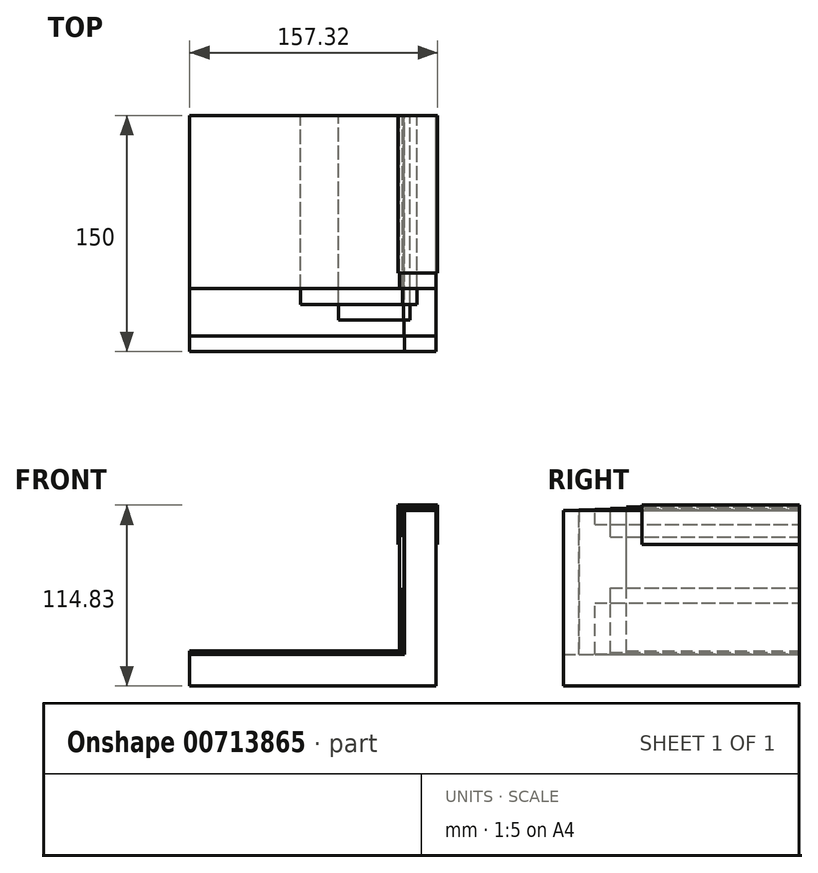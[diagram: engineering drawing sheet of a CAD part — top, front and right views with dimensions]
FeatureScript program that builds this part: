
annotation { "Feature Type Name" : "Feature", "Feature Type Description" : "" }
export const myFeature = defineFeature(function(context is Context, id is Id, definition is map)
    precondition{}
    {
        {
            var Q0;
            Q0=qCreatedBy(makeId("Front.planeOp"),FACE);
            var sketch = newSketch(context, id + "F0", { "sketchPlane" : qUnion([Q0])});
            skLineSegment(sketch, "E0", {"start": v(-78.43, -35.74) * mm, "end": v(-78.43, -55.74) * mm});
            skLineSegment(sketch, "E1", {"start": v(-78.43, -55.74) * mm, "end": v(77.9, -55.74) * mm});
            skLineSegment(sketch, "E2", {"start": v(77.9, -55.74) * mm, "end": v(77.9, 55.9) * mm});
            skLineSegment(sketch, "E3", {"start": v(77.9, 55.9) * mm, "end": v(57.9, 55.9) * mm});
            skLineSegment(sketch, "E4", {"start": v(57.9, 55.9) * mm, "end": v(57.9, -35.74) * mm});
            skLineSegment(sketch, "E5", {"start": v(57.9, -35.74) * mm, "end": v(-78.43, -35.74) * mm});
            skLineSegment(sketch, "E6", {"start": v(-78.43, -35.74) * mm, "end": v(-78.43, -35.54) * mm});
            skLineSegment(sketch, "E7", {"start": v(-78.43, -35.54) * mm, "end": v(57.7, -35.54) * mm});
            skLineSegment(sketch, "E8", {"start": v(57.7, -35.54) * mm, "end": v(57.7, 56.1) * mm});
            skLineSegment(sketch, "E9", {"start": v(57.7, 56.1) * mm, "end": v(77.9, 56.1) * mm});
            skLineSegment(sketch, "E10", {"start": v(77.9, 56.1) * mm, "end": v(77.9, 55.9) * mm});
            skLineSegment(sketch, "E11", {"start": v(16.06, -35.54) * mm, "end": v(16.06, -35.24) * mm});
            skLineSegment(sketch, "E12", {"start": v(16.06, -35.24) * mm, "end": v(57.4, -35.24) * mm});
            skLineSegment(sketch, "E13", {"start": v(57.4, -35.24) * mm, "end": v(57.4, -3.1) * mm});
            skLineSegment(sketch, "E14", {"start": v(57.4, -3.1) * mm, "end": v(57.7, -3.1) * mm});
            skLineSegment(sketch, "E15", {"start": v(-8.23, -35.54) * mm, "end": v(-8.23, -34.54) * mm});
            skLineSegment(sketch, "E16", {"start": v(-8.23, -34.54) * mm, "end": v(56.7, -34.54) * mm});
            skLineSegment(sketch, "E17", {"start": v(56.7, -34.54) * mm, "end": v(56.7, 6.5) * mm});
            skLineSegment(sketch, "E18", {"start": v(56.7, 6.5) * mm, "end": v(57.7, 6.5) * mm});
            skLineSegment(sketch, "E19", {"start": v(57.7, 46.7) * mm, "end": v(57.4, 46.7) * mm});
            skLineSegment(sketch, "E20", {"start": v(57.4, 46.7) * mm, "end": v(57.4, 56.4) * mm});
            skLineSegment(sketch, "E21", {"start": v(57.4, 56.4) * mm, "end": v(61.57, 56.4) * mm});
            skLineSegment(sketch, "E22", {"start": v(61.57, 56.4) * mm, "end": v(61.57, 56.1) * mm});
            skLineSegment(sketch, "E23", {"start": v(57.7, 38.95) * mm, "end": v(56.7, 38.95) * mm});
            skLineSegment(sketch, "E24", {"start": v(56.7, 38.95) * mm, "end": v(56.7, 57.1) * mm});
            skLineSegment(sketch, "E25", {"start": v(56.7, 57.1) * mm, "end": v(65.85, 57.1) * mm});
            skLineSegment(sketch, "E26", {"start": v(65.85, 57.1) * mm, "end": v(65.85, 56.1) * mm});
            skLineSegment(sketch, "E27", {"start": v(-78.43, -35.54) * mm, "end": v(-78.43, -33.54) * mm});
            skLineSegment(sketch, "E28", {"start": v(-78.43, -33.54) * mm, "end": v(54.7, -33.54) * mm});
            skLineSegment(sketch, "E29", {"start": v(54.7, -33.54) * mm, "end": v(54.7, 58.1) * mm});
            skLineSegment(sketch, "E30", {"start": v(54.7, 58.1) * mm, "end": v(77.9, 58.1) * mm});
            skLineSegment(sketch, "E31", {"start": v(77.9, 58.1) * mm, "end": v(77.9, 56.1) * mm});
            skLineSegment(sketch, "E32", {"start": v(54.7, 34.1) * mm, "end": v(53.7, 34.1) * mm});
            skLineSegment(sketch, "E33", {"start": v(53.7, 34.1) * mm, "end": v(53.7, 59.1) * mm});
            skLineSegment(sketch, "E34", {"start": v(53.7, 59.1) * mm, "end": v(78.9, 59.1) * mm});
            skLineSegment(sketch, "E35", {"start": v(78.9, 59.1) * mm, "end": v(78.9, 34.1) * mm});
            skLineSegment(sketch, "E36", {"start": v(78.9, 34.1) * mm, "end": v(77.9, 34.1) * mm});
            skSolve(sketch);
        }
        {
            var Q0;
            Q0=makeQuery(id+"F0.imprint","IMPRINT",FACE,{"disambiguationData":[TD([[makeQuery(id+"F0.imprint","IMPRINT",EDGE,{"derivedFrom":sQuery(id+"F0.wireOp",EDGE,"E0")}),1.0]])]});
            extrude(context, id + "F1", {"entities" : qUnion([Q0]), "depth" : 150 * mm});
        }
        {
            var Q0;
            Q0=makeQuery(id+"F0.imprint","IMPRINT",FACE,{"disambiguationData":[TD([[makeQuery(id+"F0.imprint","IMPRINT",EDGE,{"derivedFrom":sQuery(id+"F0.wireOp",EDGE,"E3")}),-1.0]])]});
            extrude(context, id + "F2", {"entities" : qUnion([Q0]), "depth" : 140 * mm});
        }
        {
            var Q0;
            {var subQ3=sQuery(id+"F0.wireOp",EDGE,"E11");Q0=makeQuery(id+"F0.imprint","IMPRINT",FACE,{"disambiguationData":[TD([[makeQuery(id+"F0.imprint","IMPRINT",EDGE,{"derivedFrom":subQ3}),-1.0]])]});}
            extrude(context, id + "F3", {"entities" : qUnion([Q0]), "depth" : 130 * mm});
        }
        {
            var Q0;
            {var subQ0=sQuery(id+"F0.wireOp",EDGE,"E19");Q0=makeQuery(id+"F0.imprint","IMPRINT",FACE,{"disambiguationData":[TD([[makeQuery(id+"F0.imprint","IMPRINT",EDGE,{"derivedFrom":subQ0}),-1.0]])]});}
            extrude(context, id + "F4", {"entities" : qUnion([Q0]), "depth" : 130 * mm});
        }
        {
            var Q0;
            {var subQ0=sQuery(id+"F0.wireOp",EDGE,"E19");Q0=makeQuery(id+"F0.imprint","IMPRINT",FACE,{"disambiguationData":[TD([[makeQuery(id+"F0.imprint","IMPRINT",EDGE,{"derivedFrom":subQ0}),1.0]])]});}
            extrude(context, id + "F5", {"entities" : qUnion([Q0]), "depth" : 120 * mm});
        }
        {
            var Q0;
            {var subQ0=sQuery(id+"F0.wireOp",EDGE,"E11");Q0=makeQuery(id+"F0.imprint","IMPRINT",FACE,{"disambiguationData":[TD([[makeQuery(id+"F0.imprint","IMPRINT",EDGE,{"derivedFrom":subQ0}),1.0]])]});}
            extrude(context, id + "F6", {"entities" : qUnion([Q0]), "depth" : 120 * mm});
        }
        {
            var Q0;
            {var subQ4=sQuery(id+"F0.wireOp",EDGE,"E15");Q0=makeQuery(id+"F0.imprint","IMPRINT",FACE,{"disambiguationData":[TD([[makeQuery(id+"F0.imprint","IMPRINT",EDGE,{"derivedFrom":subQ4}),1.0]])]});}
            extrude(context, id + "F7", {"entities" : qUnion([Q0]), "depth" : 110 * mm});
        }
        {
            var Q0;
            {var subQ3=sQuery(id+"F0.wireOp",EDGE,"E10");Q0=makeQuery(id+"F0.imprint","IMPRINT",FACE,{"disambiguationData":[TD([[makeQuery(id+"F0.imprint","IMPRINT",EDGE,{"derivedFrom":subQ3}),1.0]])]});}
            extrude(context, id + "F8", {"entities" : qUnion([Q0]), "depth" : 100 * mm});
        }
    });
